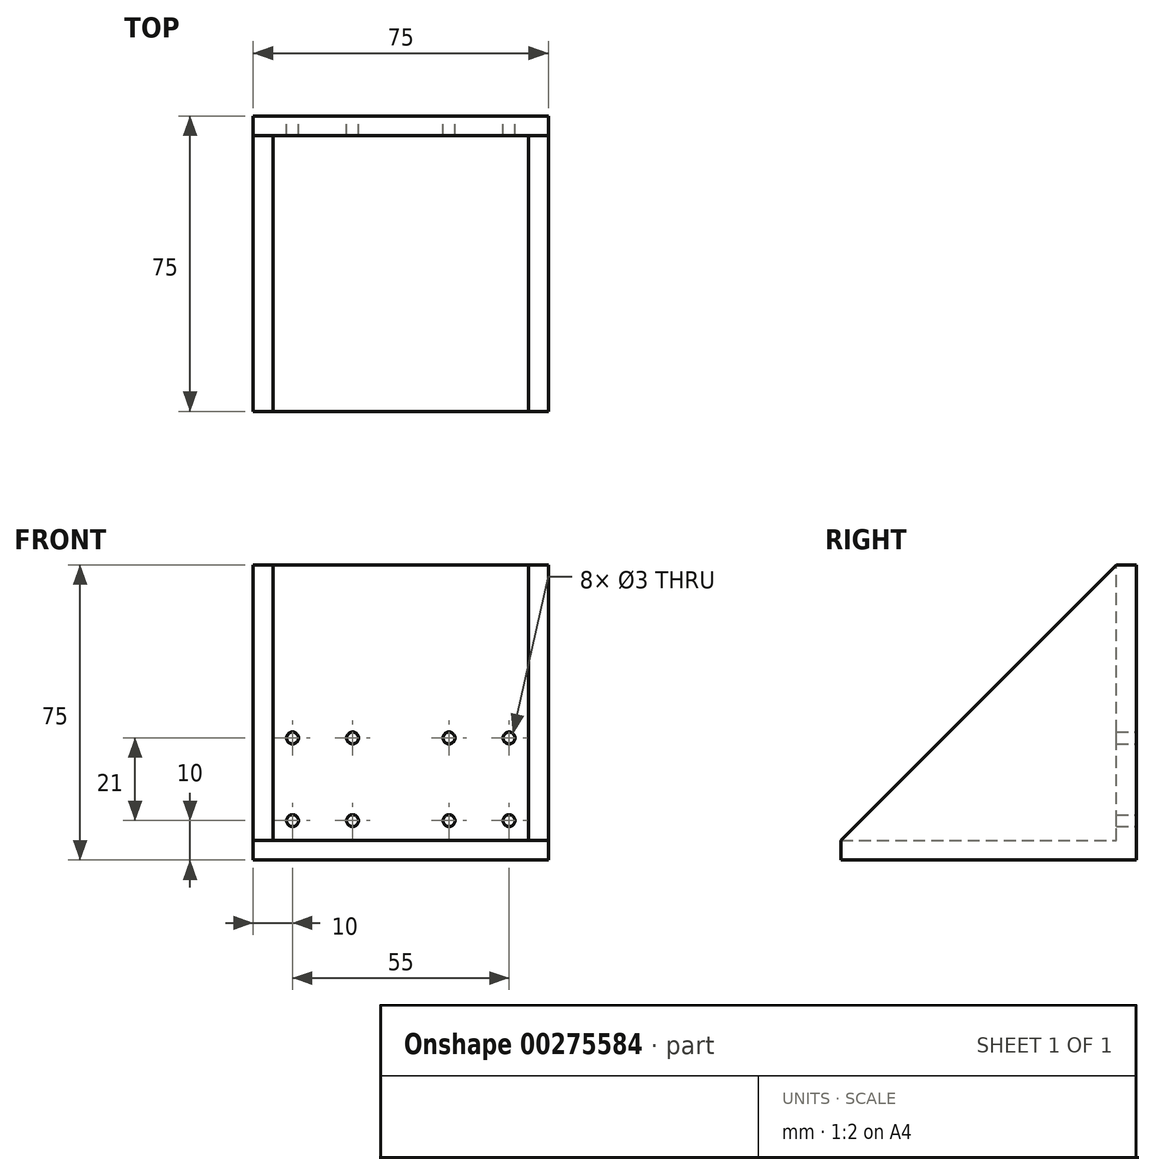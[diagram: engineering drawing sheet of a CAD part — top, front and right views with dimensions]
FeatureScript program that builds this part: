
annotation { "Feature Type Name" : "Feature", "Feature Type Description" : "" }
export const myFeature = defineFeature(function(context is Context, id is Id, definition is map)
    precondition{}
    {
        {
            var Q0;
            Q0=qCreatedBy(makeId("Right.planeOp"),FACE);
            var sketch = newSketch(context, id + "F0", { "sketchPlane" : qUnion([Q0])});
            skLineSegment(sketch, "E0", {"start": v(0, 0) * mm, "end": v(70, 0) * mm});
            skLineSegment(sketch, "E1", {"start": v(70, 0) * mm, "end": v(70, 70) * mm});
            skLineSegment(sketch, "E2", {"start": v(0, 0) * mm, "end": v(0, -5) * mm});
            skLineSegment(sketch, "E3", {"start": v(0, -5) * mm, "end": v(75, -5) * mm});
            skLineSegment(sketch, "E4", {"start": v(75, -5) * mm, "end": v(75, 70) * mm});
            skLineSegment(sketch, "E5", {"start": v(75, 70) * mm, "end": v(70, 70) * mm});
            skSolve(sketch);
        }
        {
            var Q0;
            Q0 = qSketchRegion(id + "F0", true);
            extrude(context, id + "F1", {"entities" : qUnion([Q0]), "depth" : 75 * mm});
        }
        {
            var Q0;
            Q0=makeQuery(id+"F1.opExtrude","CAP_FACE",FACE,{"disambiguationData":[OSD([sQuery(id+"F0.wireOp",EDGE,"E0"),sQuery(id+"F0.wireOp",EDGE,"E1"),sQuery(id+"F0.wireOp",EDGE,"E2"),sQuery(id+"F0.wireOp",EDGE,"E3"),sQuery(id+"F0.wireOp",EDGE,"E4"),sQuery(id+"F0.wireOp",EDGE,"E5")])],"isStart":false});
            var sketch = newSketch(context, id + "F2", { "sketchPlane" : qUnion([Q0])});
            skLineSegment(sketch, "E6", {"start": v(70, 70) * mm, "end": v(0, 0) * mm});
            skLineSegment(sketch, "E7.0", {"start": v(0, 0) * mm, "end": v(70, 0) * mm});
            skLineSegment(sketch, "E7.1", {"start": v(70, 0) * mm, "end": v(70, 70) * mm});
            skSolve(sketch);
        }
        {
            var Q0;
            Q0 = qSketchRegion(id + "F2", true);
            extrude(context, id + "F3", {"entities" : qUnion([Q0]), "operationType" : NewBodyOperationType.ADD, "oppositeDirection" : true, "depth" : 5 * mm});
        }
        {
            var Q0;
            Q0=makeQuery(id+"F1.opExtrude","CAP_FACE",FACE,{"disambiguationData":[OSD([sQuery(id+"F0.wireOp",EDGE,"E0"),sQuery(id+"F0.wireOp",EDGE,"E1"),sQuery(id+"F0.wireOp",EDGE,"E2"),sQuery(id+"F0.wireOp",EDGE,"E3"),sQuery(id+"F0.wireOp",EDGE,"E4"),sQuery(id+"F0.wireOp",EDGE,"E5")])],"isStart":true});
            var sketch = newSketch(context, id + "F4", { "sketchPlane" : qUnion([Q0])});
            skLineSegment(sketch, "E8.0", {"start": v(-70, 0) * mm, "end": v(-70, 70) * mm});
            skLineSegment(sketch, "E8.1", {"start": v(0, 0) * mm, "end": v(-70, 0) * mm});
            skLineSegment(sketch, "E9", {"start": v(-70, 70) * mm, "end": v(0, 0) * mm});
            skSolve(sketch);
        }
        {
            var Q0;
            Q0 = qSketchRegion(id + "F4", true);
            extrude(context, id + "F5", {"entities" : qUnion([Q0]), "operationType" : NewBodyOperationType.ADD, "oppositeDirection" : true, "depth" : 5 * mm});
        }
        {
            var Q0;
            Q0=makeQuery(id+"F1.opExtrude","SWEPT_FACE",FACE,{"disambiguationData":[OSD([sQuery(id+"F0.wireOp",EDGE,"E4")])]});
            var sketch = newSketch(context, id + "F6", { "sketchPlane" : qUnion([Q0])});
            skLineSegment(sketch, "E10", {"start": v(-37.5, 70) * mm, "end": v(-37.5, -5) * mm, "construction": true});
            skLineSegment(sketch, "E11.bottom", {"start": v(-65, 26) * mm, "end": v(-49.75, 26) * mm, "construction": true});
            skLineSegment(sketch, "E11.top", {"start": v(-65, 5) * mm, "end": v(-49.75, 5) * mm, "construction": true});
            skLineSegment(sketch, "E11.left", {"start": v(-65, 26) * mm, "end": v(-65, 5) * mm, "construction": true});
            skLineSegment(sketch, "E11.right", {"start": v(-49.75, 26) * mm, "end": v(-49.75, 5) * mm, "construction": true});
            skCircle(sketch, "E12", {"center": v(-65, 26) * mm, "radius": 1.5 * mm});
            skCircle(sketch, "E13", {"center": v(-49.75, 26) * mm, "radius": 1.5 * mm});
            skCircle(sketch, "E14", {"center": v(-49.75, 5) * mm, "radius": 1.5 * mm});
            skCircle(sketch, "E15", {"center": v(-65, 5) * mm, "radius": 1.5 * mm});
            skCircle(sketch, "E16.MirrorC", {"center": v(-10, 5) * mm, "radius": 1.5 * mm});
            skCircle(sketch, "E17.MirrorC", {"center": v(-25.25, 5) * mm, "radius": 1.5 * mm});
            skCircle(sketch, "E18.MirrorC", {"center": v(-25.25, 26) * mm, "radius": 1.5 * mm});
            skCircle(sketch, "E19.MirrorC", {"center": v(-10, 26) * mm, "radius": 1.5 * mm});
            skSolve(sketch);
        }
        {
            var Q0;
            Q0 = qSketchRegion(id + "F6", true);
            var Q1;
            Q1=makeQuery(id+"F1.opExtrude","SWEPT_FACE",FACE,{"disambiguationData":[OSD([sQuery(id+"F0.wireOp",EDGE,"E1")])]});
            extrude(context, id + "F7", {"entities" : qUnion([Q0]), "operationType" : NewBodyOperationType.REMOVE, "endBound" : BoundingType.UP_TO_SURFACE, "oppositeDirection" : true, "endBoundEntityFace" : qUnion([Q1]), "depth" : 25 * mm});
        }
    });
